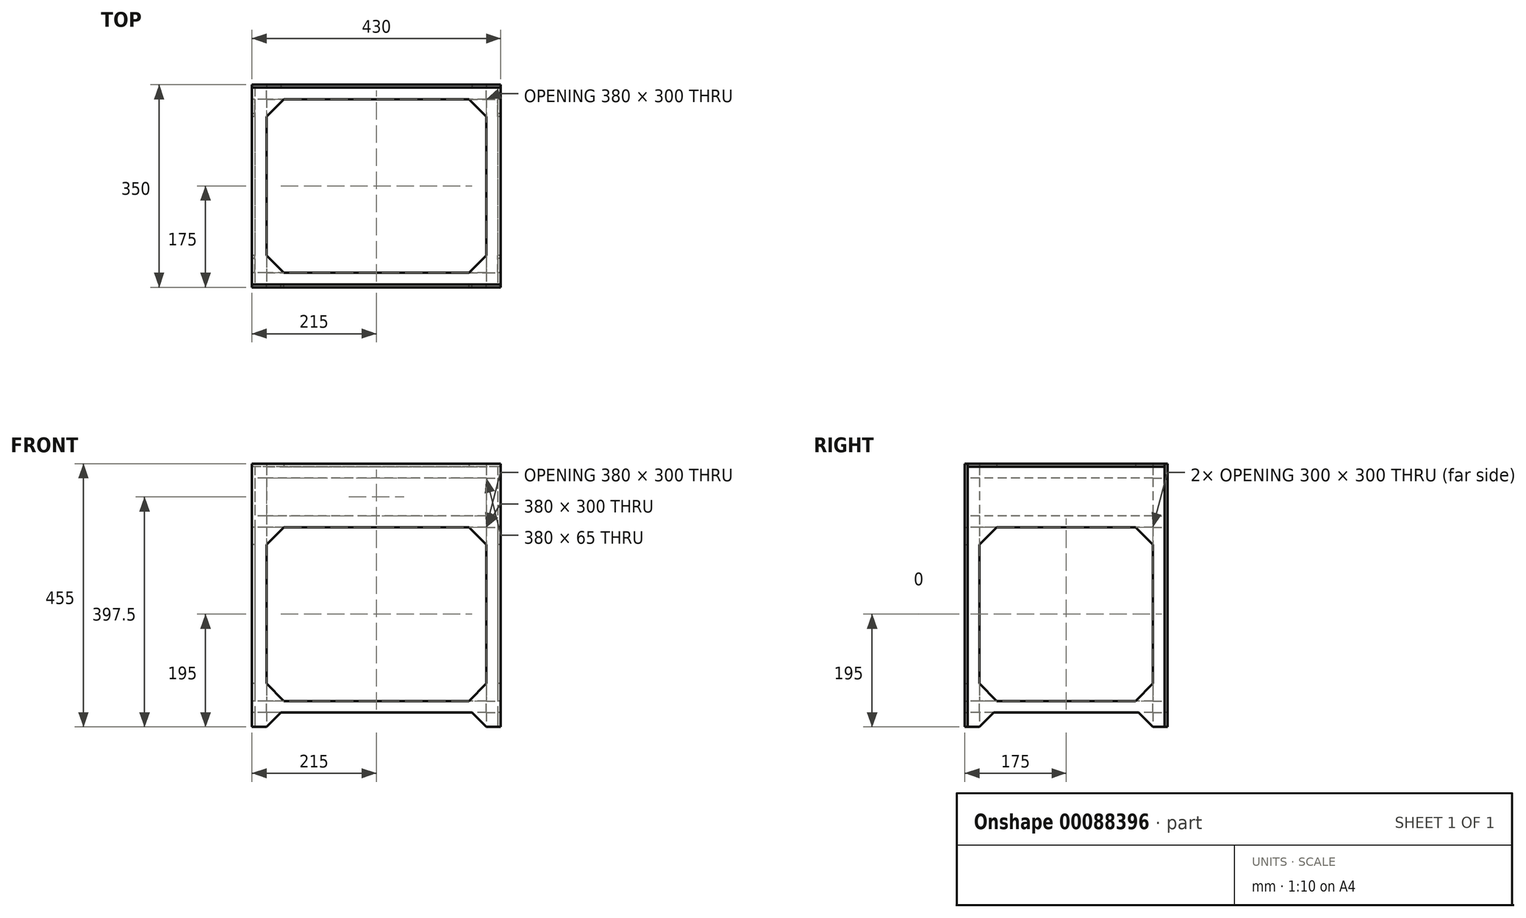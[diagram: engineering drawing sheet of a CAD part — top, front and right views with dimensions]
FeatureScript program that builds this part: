
annotation { "Feature Type Name" : "Feature", "Feature Type Description" : "" }
export const myFeature = defineFeature(function(context is Context, id is Id, definition is map)
    precondition{}
    {
        {
            assignVariable(context, id + "F0", {"name" : "thick", "anyValue" : 5});
        }
        {
            var Q0;
            Q0=qCreatedBy(makeId("Top.planeOp"),FACE);
            var sketch = newSketch(context, id + "F1", { "sketchPlane" : qUnion([Q0])});
            skLineSegment(sketch, "E0.bottom", {"start": v(190, 150) * mm, "end": v(-190, 150) * mm});
            skLineSegment(sketch, "E0.top", {"start": v(190, -150) * mm, "end": v(-190, -150) * mm});
            skLineSegment(sketch, "E0.left", {"start": v(190, 150) * mm, "end": v(190, -150) * mm});
            skLineSegment(sketch, "E0.right", {"start": v(-190, 150) * mm, "end": v(-190, -150) * mm});
            skPoint(sketch, "E0.middle", {"position": v(0, 0) * mm});
            skLineSegment(sketch, "E1.0", {"start": v(210, 170) * mm, "end": v(-210, 170) * mm});
            skLineSegment(sketch, "E1.1", {"start": v(210, 170) * mm, "end": v(210, -170) * mm});
            skLineSegment(sketch, "E1.2", {"start": v(210, -170) * mm, "end": v(-210, -170) * mm});
            skLineSegment(sketch, "E1.3", {"start": v(-210, 170) * mm, "end": v(-210, -170) * mm});
            skLineSegment(sketch, "E2", {"start": v(190, -150) * mm, "end": v(190, -170) * mm});
            skLineSegment(sketch, "E3", {"start": v(-190, -150) * mm, "end": v(-190, -170) * mm});
            skLineSegment(sketch, "E4", {"start": v(-190, 150) * mm, "end": v(-190, 170) * mm});
            skLineSegment(sketch, "E5", {"start": v(190, 150) * mm, "end": v(190, 170) * mm});
            skLineSegment(sketch, "E6", {"start": v(190, 150) * mm, "end": v(210, 150) * mm});
            skLineSegment(sketch, "E7", {"start": v(190, -150) * mm, "end": v(210, -150) * mm});
            skLineSegment(sketch, "E8", {"start": v(-190, -150) * mm, "end": v(-210, -150) * mm});
            skLineSegment(sketch, "E9", {"start": v(-190, 150) * mm, "end": v(-210, 150) * mm});
            skSolve(sketch);
        }
        {
            var Q0;
            Q0=makeQuery(id+"F1.imprint","IMPRINT",FACE,{"disambiguationData":[TD([[makeQuery(id+"F1.imprint","IMPRINT",EDGE,{"derivedFrom":sQuery(id+"F1.wireOp",EDGE,"E0.right")}),-1.0]])]});
            var Q1;
            Q1=makeQuery(id+"F1.imprint","IMPRINT",FACE,{"disambiguationData":[TD([[makeQuery(id+"F1.imprint","IMPRINT",EDGE,{"derivedFrom":sQuery(id+"F1.wireOp",EDGE,"E0.bottom")}),-1.0]])]});
            var Q2;
            Q2=makeQuery(id+"F1.imprint","IMPRINT",FACE,{"disambiguationData":[TD([[makeQuery(id+"F1.imprint","IMPRINT",EDGE,{"derivedFrom":sQuery(id+"F1.wireOp",EDGE,"E0.left")}),1.0]])]});
            var Q3;
            Q3=makeQuery(id+"F1.imprint","IMPRINT",FACE,{"disambiguationData":[TD([[makeQuery(id+"F1.imprint","IMPRINT",EDGE,{"derivedFrom":sQuery(id+"F1.wireOp",EDGE,"E0.top")}),1.0]])]});
            extrude(context, id + "F2", {"entities" : qUnion([Q0, Q1, Q2, Q3]), "depth" : 20 * mm});
        }
        {
            var Q0;
            {var subQ3=sQuery(id+"F1.wireOp",EDGE,"E3");Q0=makeQuery(id+"F1.imprint","IMPRINT",FACE,{"disambiguationData":[TD([[makeQuery(id+"F1.imprint","IMPRINT",EDGE,{"derivedFrom":subQ3}),-1.0]])]});}
            var Q1;
            {var subQ4=sQuery(id+"F1.wireOp",EDGE,"E2");Q1=makeQuery(id+"F1.imprint","IMPRINT",FACE,{"disambiguationData":[TD([[makeQuery(id+"F1.imprint","IMPRINT",EDGE,{"derivedFrom":subQ4}),1.0]])]});}
            var Q2;
            {var subQ3=sQuery(id+"F1.wireOp",EDGE,"E4");Q2=makeQuery(id+"F1.imprint","IMPRINT",FACE,{"disambiguationData":[TD([[makeQuery(id+"F1.imprint","IMPRINT",EDGE,{"derivedFrom":subQ3}),1.0]])]});}
            var Q3;
            {var subQ3=sQuery(id+"F1.wireOp",EDGE,"E5");Q3=makeQuery(id+"F1.imprint","IMPRINT",FACE,{"disambiguationData":[TD([[makeQuery(id+"F1.imprint","IMPRINT",EDGE,{"derivedFrom":subQ3}),-1.0]])]});}
            extrude(context, id + "F3", {"entities" : qUnion([Q0, Q1, Q2, Q3]), "operationType" : NewBodyOperationType.ADD, "depth" : 105 * mm, "hasSecondDirection" : true, "secondDirectionOppositeDirection" : true, "secondDirectionDepth" : 345 * mm});
        }
        {
            var Q0;
            Q0=makeQuery(id+"F1.imprint","IMPRINT",FACE,{"disambiguationData":[TD([[makeQuery(id+"F1.imprint","IMPRINT",EDGE,{"derivedFrom":sQuery(id+"F1.wireOp",EDGE,"E0.right")}),-1.0]])]});
            var Q1;
            Q1=makeQuery(id+"F1.imprint","IMPRINT",FACE,{"disambiguationData":[TD([[makeQuery(id+"F1.imprint","IMPRINT",EDGE,{"derivedFrom":sQuery(id+"F1.wireOp",EDGE,"E0.bottom")}),-1.0]])]});
            var Q2;
            Q2=makeQuery(id+"F1.imprint","IMPRINT",FACE,{"disambiguationData":[TD([[makeQuery(id+"F1.imprint","IMPRINT",EDGE,{"derivedFrom":sQuery(id+"F1.wireOp",EDGE,"E0.left")}),1.0]])]});
            var Q3;
            Q3=makeQuery(id+"F1.imprint","IMPRINT",FACE,{"disambiguationData":[TD([[makeQuery(id+"F1.imprint","IMPRINT",EDGE,{"derivedFrom":sQuery(id+"F1.wireOp",EDGE,"E0.top")}),1.0]])]});
            var Q4;
            Q4=makeQuery(id+"F3.opExtrude","CAP_FACE",FACE,{"disambiguationData":[OSD([sQuery(id+"F1.wireOp",EDGE,"E1.2"),sQuery(id+"F1.wireOp",EDGE,"E1.3"),sQuery(id+"F1.wireOp",EDGE,"E3"),sQuery(id+"F1.wireOp",EDGE,"E8")])],"isStart":false});
            extrude(context, id + "F4", {"entities" : qUnion([Q0, Q1, Q2, Q3]), "operationType" : NewBodyOperationType.ADD, "endBound" : BoundingType.UP_TO_SURFACE, "endBoundEntityFace" : qUnion([Q4]), "depth" : 50 * mm, "hasSecondDirection" : true, "secondDirectionOppositeDirection" : false, "secondDirectionDepth" : 85 * mm});
        }
        {
            var Q0;
            Q0=makeQuery(id+"F1.imprint","IMPRINT",FACE,{"disambiguationData":[TD([[makeQuery(id+"F1.imprint","IMPRINT",EDGE,{"derivedFrom":sQuery(id+"F1.wireOp",EDGE,"E0.right")}),-1.0]])]});
            var Q1;
            Q1=makeQuery(id+"F1.imprint","IMPRINT",FACE,{"disambiguationData":[TD([[makeQuery(id+"F1.imprint","IMPRINT",EDGE,{"derivedFrom":sQuery(id+"F1.wireOp",EDGE,"E0.bottom")}),-1.0]])]});
            var Q2;
            Q2=makeQuery(id+"F1.imprint","IMPRINT",FACE,{"disambiguationData":[TD([[makeQuery(id+"F1.imprint","IMPRINT",EDGE,{"derivedFrom":sQuery(id+"F1.wireOp",EDGE,"E0.left")}),1.0]])]});
            var Q3;
            Q3=makeQuery(id+"F1.imprint","IMPRINT",FACE,{"disambiguationData":[TD([[makeQuery(id+"F1.imprint","IMPRINT",EDGE,{"derivedFrom":sQuery(id+"F1.wireOp",EDGE,"E0.top")}),1.0]])]});
            extrude(context, id + "F5", {"entities" : qUnion([Q0, Q1, Q2, Q3]), "operationType" : NewBodyOperationType.ADD, "oppositeDirection" : true, "depth" : 320 * mm, "hasSecondDirection" : true, "secondDirectionOppositeDirection" : true, "secondDirectionDepth" : 300 * mm});
        }
        {
            var Q0;
            {var subQ0=sQuery(id+"F1.wireOp",EDGE,"E1.2");Q0=makeQuery(id+"F5.boolean.opBoolean","MERGE",FACE,{"derivedFrom":[makeQuery(id+"F4.boolean.opBoolean","MERGE",FACE,{"derivedFrom":[makeQuery(id+"F3.boolean.opBoolean","MERGE",FACE,{"derivedFrom":[makeQuery(id+"F2.opExtrude","SWEPT_FACE",FACE,{"disambiguationData":[OSD([subQ0])]}),makeQuery(id+"F3.opExtrude","SWEPT_FACE",FACE,{"disambiguationData":[OSD([subQ0]),TDD([makeQuery(id+"F1.imprint","IMPRINT",EDGE,{"disambiguationData":[TD([[makeQuery(id+"F1.imprint","INTERSECT",VERTEX,{"derivedFrom":[sQuery(id+"F1.wireOp",EDGE,"E1.1"),subQ0]}),-1.0]])],"derivedFrom":subQ0})])]}),makeQuery(id+"F3.opExtrude","SWEPT_FACE",FACE,{"disambiguationData":[OSD([subQ0]),TDD([makeQuery(id+"F1.imprint","IMPRINT",EDGE,{"disambiguationData":[TD([[makeQuery(id+"F1.imprint","INTERSECT",VERTEX,{"derivedFrom":[subQ0,sQuery(id+"F1.wireOp",EDGE,"E1.3")]}),1.0]])],"derivedFrom":subQ0})])]})]}),makeQuery(id+"F4.opExtrude","SWEPT_FACE",FACE,{"disambiguationData":[OSD([subQ0])]})]}),makeQuery(id+"F5.opExtrude","SWEPT_FACE",FACE,{"disambiguationData":[OSD([subQ0])]})]});}
            var sketch = newSketch(context, id + "F6", { "sketchPlane" : qUnion([Q0])});
            skLineSegment(sketch, "E10.0.0", {"start": v(-190, -320) * mm, "end": v(190, -320) * mm});
            skLineSegment(sketch, "E10.0.1", {"start": v(190, -320) * mm, "end": v(190, -345) * mm});
            skLineSegment(sketch, "E10.0.2", {"start": v(190, -345) * mm, "end": v(210, -345) * mm});
            skLineSegment(sketch, "E10.0.3", {"start": v(210, -345) * mm, "end": v(210, 105) * mm});
            skLineSegment(sketch, "E10.0.4", {"start": v(210, 105) * mm, "end": v(-210, 105) * mm});
            skLineSegment(sketch, "E10.0.5", {"start": v(-210, 105) * mm, "end": v(-210, -345) * mm});
            skLineSegment(sketch, "E10.0.6", {"start": v(-210, -345) * mm, "end": v(-190, -345) * mm});
            skLineSegment(sketch, "E10.0.7", {"start": v(-190, -345) * mm, "end": v(-190, -320) * mm});
            skLineSegment(sketch, "E11.0", {"start": v(190, 85) * mm, "end": v(-190, 85) * mm});
            skLineSegment(sketch, "E12.0", {"start": v(-190, 85) * mm, "end": v(-190, 20) * mm});
            skLineSegment(sketch, "E13.0", {"start": v(190, 20) * mm, "end": v(-190, 20) * mm});
            skLineSegment(sketch, "E14.0", {"start": v(190, 85) * mm, "end": v(190, 20) * mm});
            skLineSegment(sketch, "E15.0", {"start": v(-190, 0) * mm, "end": v(-190, -300) * mm});
            skLineSegment(sketch, "E16.0", {"start": v(190, -300) * mm, "end": v(-190, -300) * mm});
            skLineSegment(sketch, "E17.0", {"start": v(190, 0) * mm, "end": v(190, -300) * mm});
            skLineSegment(sketch, "E18", {"start": v(-160, 0) * mm, "end": v(-190, -30) * mm});
            skLineSegment(sketch, "E19", {"start": v(160, 0) * mm, "end": v(190, -30) * mm});
            skLineSegment(sketch, "E20", {"start": v(190, -270) * mm, "end": v(160, -300) * mm});
            skLineSegment(sketch, "E21", {"start": v(-190, -270) * mm, "end": v(-160, -300) * mm});
            skLineSegment(sketch, "E22", {"start": v(-165, -320) * mm, "end": v(-190, -345) * mm});
            skLineSegment(sketch, "E23", {"start": v(165, -320) * mm, "end": v(190, -345) * mm});
            skLineSegment(sketch, "E24.0", {"start": v(-215, 110) * mm, "end": v(-215, -345) * mm});
            skLineSegment(sketch, "E24.1", {"start": v(215, 110) * mm, "end": v(-215, 110) * mm});
            skLineSegment(sketch, "E24.2", {"start": v(215, -345) * mm, "end": v(215, 110) * mm});
            skLineSegment(sketch, "E25", {"start": v(-215, -345) * mm, "end": v(-210, -345) * mm});
            skLineSegment(sketch, "E26", {"start": v(210, -345) * mm, "end": v(215, -345) * mm});
            skLineSegment(sketch, "E27.0", {"start": v(190, 0) * mm, "end": v(-190, 0) * mm});
            skSolve(sketch);
        }
        {
            var Q0;
            {var subQ20=sQuery(id+"F6.wireOp",EDGE,"E10.0.1");Q0=makeQuery(id+"F6.imprint","IMPRINT",FACE,{"disambiguationData":[TD([[makeQuery(id+"F6.imprint","IMPRINT",EDGE,{"derivedFrom":subQ20}),1.0]])]});}
            var Q1;
            Q1=makeQuery(id+"F6.imprint","IMPRINT",FACE,{"disambiguationData":[TD([[makeQuery(id+"F6.imprint","IMPRINT",EDGE,{"derivedFrom":sQuery(id+"F6.wireOp",EDGE,"E10.0.3")}),1.0]])]});
            var Q2;
            {var subQ3=sQuery(id+"F6.wireOp",EDGE,"E19");Q2=makeQuery(id+"F6.imprint","IMPRINT",FACE,{"disambiguationData":[TD([[makeQuery(id+"F6.imprint","IMPRINT",EDGE,{"derivedFrom":subQ3}),1.0]])]});}
            var Q3;
            {var subQ3=sQuery(id+"F6.wireOp",EDGE,"E18");Q3=makeQuery(id+"F6.imprint","IMPRINT",FACE,{"disambiguationData":[TD([[makeQuery(id+"F6.imprint","IMPRINT",EDGE,{"derivedFrom":subQ3}),-1.0]])]});}
            var Q4;
            {var subQ3=sQuery(id+"F6.wireOp",EDGE,"E20");Q4=makeQuery(id+"F6.imprint","IMPRINT",FACE,{"disambiguationData":[TD([[makeQuery(id+"F6.imprint","IMPRINT",EDGE,{"derivedFrom":subQ3}),1.0]])]});}
            var Q5;
            {var subQ0=sQuery(id+"F6.wireOp",EDGE,"E10.0.1");Q5=makeQuery(id+"F6.imprint","IMPRINT",FACE,{"disambiguationData":[TD([[makeQuery(id+"F6.imprint","IMPRINT",EDGE,{"derivedFrom":subQ0}),-1.0]])]});}
            var Q6;
            {var subQ3=sQuery(id+"F6.wireOp",EDGE,"E21");Q6=makeQuery(id+"F6.imprint","IMPRINT",FACE,{"disambiguationData":[TD([[makeQuery(id+"F6.imprint","IMPRINT",EDGE,{"derivedFrom":subQ3}),-1.0]])]});}
            var Q7;
            {var subQ0=sQuery(id+"F6.wireOp",EDGE,"E10.0.7");Q7=makeQuery(id+"F6.imprint","IMPRINT",FACE,{"disambiguationData":[TD([[makeQuery(id+"F6.imprint","IMPRINT",EDGE,{"derivedFrom":subQ0}),1.0]])]});}
            var Q8;
            Q8=makeQuery(id+"F6.imprint","IMPRINT",FACE,{"disambiguationData":[TD([[makeQuery(id+"F6.imprint","IMPRINT",EDGE,{"derivedFrom":sQuery(id+"F6.wireOp",EDGE,"E11.0")}),1.0]])]});
            extrude(context, id + "F7", {"entities" : qUnion([Q0, Q1, Q2, Q3, Q4, Q5, Q6, Q7, Q8]), "depth" : (getVariable(context, 'thick')) * mm});
        }
        {
            var Q0;
            {var subQ0=sQuery(id+"F1.wireOp",EDGE,"E1.0");Q0=makeQuery(id+"F5.boolean.opBoolean","MERGE",FACE,{"derivedFrom":[makeQuery(id+"F4.boolean.opBoolean","MERGE",FACE,{"derivedFrom":[makeQuery(id+"F3.boolean.opBoolean","MERGE",FACE,{"derivedFrom":[makeQuery(id+"F2.opExtrude","SWEPT_FACE",FACE,{"disambiguationData":[OSD([subQ0])]}),makeQuery(id+"F3.opExtrude","SWEPT_FACE",FACE,{"disambiguationData":[OSD([subQ0]),TDD([makeQuery(id+"F1.imprint","IMPRINT",EDGE,{"disambiguationData":[TD([[makeQuery(id+"F1.imprint","INTERSECT",VERTEX,{"derivedFrom":[subQ0,sQuery(id+"F1.wireOp",EDGE,"E1.1")]}),-1.0]])],"derivedFrom":subQ0})])]}),makeQuery(id+"F3.opExtrude","SWEPT_FACE",FACE,{"disambiguationData":[OSD([subQ0]),TDD([makeQuery(id+"F1.imprint","IMPRINT",EDGE,{"disambiguationData":[TD([[makeQuery(id+"F1.imprint","INTERSECT",VERTEX,{"derivedFrom":[subQ0,sQuery(id+"F1.wireOp",EDGE,"E1.3")]}),1.0]])],"derivedFrom":subQ0})])]})]}),makeQuery(id+"F4.opExtrude","SWEPT_FACE",FACE,{"disambiguationData":[OSD([subQ0])]})]}),makeQuery(id+"F5.opExtrude","SWEPT_FACE",FACE,{"disambiguationData":[OSD([subQ0])]})]});}
            var sketch = newSketch(context, id + "F8", { "sketchPlane" : qUnion([Q0])});
            skLineSegment(sketch, "E28.0.0", {"start": v(-190, -320) * mm, "end": v(190, -320) * mm});
            skLineSegment(sketch, "E28.0.1", {"start": v(190, -320) * mm, "end": v(190, -345) * mm});
            skLineSegment(sketch, "E28.0.2", {"start": v(190, -345) * mm, "end": v(210, -345) * mm});
            skLineSegment(sketch, "E28.0.3", {"start": v(210, -345) * mm, "end": v(210, 105) * mm});
            skLineSegment(sketch, "E28.0.4", {"start": v(210, 105) * mm, "end": v(-210, 105) * mm});
            skLineSegment(sketch, "E28.0.5", {"start": v(-210, 105) * mm, "end": v(-210, -345) * mm});
            skLineSegment(sketch, "E28.0.6", {"start": v(-210, -345) * mm, "end": v(-190, -345) * mm});
            skLineSegment(sketch, "E28.0.7", {"start": v(-190, -345) * mm, "end": v(-190, -320) * mm});
            skLineSegment(sketch, "E29", {"start": v(190, -345) * mm, "end": v(165, -320) * mm});
            skLineSegment(sketch, "E30", {"start": v(-190, -345) * mm, "end": v(-165, -320) * mm});
            skLineSegment(sketch, "E31.0", {"start": v(-215, 110) * mm, "end": v(-215, -345) * mm});
            skLineSegment(sketch, "E31.1", {"start": v(215, 110) * mm, "end": v(-215, 110) * mm});
            skLineSegment(sketch, "E31.2", {"start": v(215, -345) * mm, "end": v(215, 110) * mm});
            skLineSegment(sketch, "E32", {"start": v(-210, -345) * mm, "end": v(-215, -345) * mm});
            skLineSegment(sketch, "E33", {"start": v(210, -345) * mm, "end": v(215, -345) * mm});
            skSolve(sketch);
        }
        {
            var Q0;
            {var subQ0=sQuery(id+"F8.wireOp",EDGE,"E28.0.1");Q0=makeQuery(id+"F8.imprint","IMPRINT",FACE,{"disambiguationData":[TD([[makeQuery(id+"F8.imprint","IMPRINT",EDGE,{"derivedFrom":subQ0}),1.0]])]});}
            var Q1;
            {var subQ0=sQuery(id+"F1.wireOp",EDGE,"E1.0");Q1=makeQuery(id+"F8.imprint","IMPRINT",FACE,{"disambiguationData":[TD([[makeQuery(id+"F8.imprint","IMPRINT",EDGE,{"derivedFrom":makeQuery(id+"F2.opExtrude","CAP_EDGE",EDGE,{"disambiguationData":[OSD([subQ0])],"isStart":false})}),1.0]])]});}
            var Q2;
            {var subQ0=sQuery(id+"F1.wireOp",EDGE,"E1.0");Q2=makeQuery(id+"F8.imprint","IMPRINT",FACE,{"disambiguationData":[TD([[makeQuery(id+"F8.imprint","IMPRINT",EDGE,{"derivedFrom":makeQuery(id+"F2.opExtrude","CAP_EDGE",EDGE,{"disambiguationData":[OSD([subQ0])],"isStart":true})}),-1.0]])]});}
            var Q3;
            Q3=makeQuery(id+"F8.imprint","IMPRINT",FACE,{"disambiguationData":[TD([[makeQuery(id+"F8.imprint","IMPRINT",EDGE,{"derivedFrom":sQuery(id+"F8.wireOp",EDGE,"E28.0.3")}),1.0]])]});
            var Q4;
            {var subQ0=sQuery(id+"F8.wireOp",EDGE,"E28.0.1");Q4=makeQuery(id+"F8.imprint","IMPRINT",FACE,{"disambiguationData":[TD([[makeQuery(id+"F8.imprint","IMPRINT",EDGE,{"derivedFrom":subQ0}),-1.0]])]});}
            var Q5;
            {var subQ0=sQuery(id+"F8.wireOp",EDGE,"E28.0.7");Q5=makeQuery(id+"F8.imprint","IMPRINT",FACE,{"disambiguationData":[TD([[makeQuery(id+"F8.imprint","IMPRINT",EDGE,{"derivedFrom":subQ0}),1.0]])]});}
            extrude(context, id + "F9", {"entities" : qUnion([Q0, Q1, Q2, Q3, Q4, Q5]), "depth" : (getVariable(context, 'thick')) * mm});
        }
        {
            var Q0;
            {var subQ0=sQuery(id+"F1.wireOp",EDGE,"E9");var subQ1=sQuery(id+"F1.wireOp",EDGE,"E8");var subQ2=sQuery(id+"F1.wireOp",EDGE,"E1.3");var subQ3=sQuery(id+"F1.wireOp",EDGE,"E7");var subQ4=sQuery(id+"F1.wireOp",EDGE,"E6");var subQ5=sQuery(id+"F1.wireOp",EDGE,"E1.1");var subQ6=sQuery(id+"F1.wireOp",EDGE,"E3");var subQ7=sQuery(id+"F1.wireOp",EDGE,"E2");var subQ8=sQuery(id+"F1.wireOp",EDGE,"E1.2");var subQ9=sQuery(id+"F1.wireOp",EDGE,"E5");var subQ10=sQuery(id+"F1.wireOp",EDGE,"E4");var subQ11=sQuery(id+"F1.wireOp",EDGE,"E1.0");Q0=makeQuery(id+"F4.boolean.opBoolean","MERGE",FACE,{"derivedFrom":[makeQuery(id+"F3.opExtrude","CAP_FACE",FACE,{"disambiguationData":[OSD([subQ11,subQ5,subQ9,subQ4])],"isStart":false}),makeQuery(id+"F3.opExtrude","CAP_FACE",FACE,{"disambiguationData":[OSD([subQ11,subQ2,subQ10,subQ0])],"isStart":false}),makeQuery(id+"F3.opExtrude","CAP_FACE",FACE,{"disambiguationData":[OSD([subQ5,subQ8,subQ7,subQ3])],"isStart":false}),makeQuery(id+"F3.opExtrude","CAP_FACE",FACE,{"disambiguationData":[OSD([subQ8,subQ2,subQ6,subQ1])],"isStart":false}),makeQuery(id+"F4.opExtrude","CAP_FACE",FACE,{"disambiguationData":[OSD([sQuery(id+"F1.wireOp",EDGE,"E0.bottom"),subQ11,subQ10,subQ9])],"isStart":false}),makeQuery(id+"F4.opExtrude","CAP_FACE",FACE,{"disambiguationData":[OSD([sQuery(id+"F1.wireOp",EDGE,"E0.top"),subQ8,subQ7,subQ6])],"isStart":false}),makeQuery(id+"F4.opExtrude","CAP_FACE",FACE,{"disambiguationData":[OSD([sQuery(id+"F1.wireOp",EDGE,"E0.left"),subQ5,subQ4,subQ3])],"isStart":false}),makeQuery(id+"F4.opExtrude","CAP_FACE",FACE,{"disambiguationData":[OSD([sQuery(id+"F1.wireOp",EDGE,"E0.right"),subQ2,subQ1,subQ0])],"isStart":false})]});}
            var sketch = newSketch(context, id + "F10", { "sketchPlane" : qUnion([Q0])});
            skLineSegment(sketch, "E34.0.0", {"start": v(210, -170) * mm, "end": v(210, 170) * mm});
            skLineSegment(sketch, "E34.0.1", {"start": v(210, 170) * mm, "end": v(-210, 170) * mm});
            skLineSegment(sketch, "E34.0.2", {"start": v(-210, 170) * mm, "end": v(-210, -170) * mm});
            skLineSegment(sketch, "E34.0.3", {"start": v(-210, -170) * mm, "end": v(210, -170) * mm});
            skLineSegment(sketch, "E35.0", {"start": v(215, -170) * mm, "end": v(215, 170) * mm});
            skLineSegment(sketch, "E36.0", {"start": v(-215, 170) * mm, "end": v(-215, -170) * mm});
            skLineSegment(sketch, "E37", {"start": v(-215, -170) * mm, "end": v(-210, -170) * mm});
            skLineSegment(sketch, "E38", {"start": v(-215, 170) * mm, "end": v(-210, 170) * mm});
            skLineSegment(sketch, "E39", {"start": v(210, 170) * mm, "end": v(215, 170) * mm});
            skLineSegment(sketch, "E40", {"start": v(210, -170) * mm, "end": v(215, -170) * mm});
            skLineSegment(sketch, "E41.0", {"start": v(-190, 150) * mm, "end": v(-190, -150) * mm});
            skLineSegment(sketch, "E42.0", {"start": v(190, -150) * mm, "end": v(-190, -150) * mm});
            skLineSegment(sketch, "E43.0", {"start": v(190, -150) * mm, "end": v(190, 150) * mm});
            skLineSegment(sketch, "E44.0", {"start": v(190, 150) * mm, "end": v(-190, 150) * mm});
            skLineSegment(sketch, "E45", {"start": v(-190, -120) * mm, "end": v(-160, -150) * mm});
            skLineSegment(sketch, "E46", {"start": v(-190, 120) * mm, "end": v(-160, 150) * mm});
            skLineSegment(sketch, "E47", {"start": v(160, 150) * mm, "end": v(190, 120) * mm});
            skLineSegment(sketch, "E48", {"start": v(160, -150) * mm, "end": v(190, -120) * mm});
            skSolve(sketch);
        }
        {
            var Q0;
            Q0=makeQuery(id+"F10.imprint","IMPRINT",FACE,{"disambiguationData":[TD([[makeQuery(id+"F10.imprint","IMPRINT",EDGE,{"derivedFrom":sQuery(id+"F10.wireOp",EDGE,"E34.0.0")}),-1.0]])]});
            var Q1;
            Q1=makeQuery(id+"F10.imprint","IMPRINT",FACE,{"disambiguationData":[TD([[makeQuery(id+"F10.imprint","IMPRINT",EDGE,{"derivedFrom":sQuery(id+"F10.wireOp",EDGE,"E34.0.2")}),-1.0]])]});
            var Q2;
            Q2=makeQuery(id+"F10.imprint","IMPRINT",FACE,{"disambiguationData":[TD([[makeQuery(id+"F10.imprint","IMPRINT",EDGE,{"derivedFrom":sQuery(id+"F10.wireOp",EDGE,"E34.0.0")}),1.0]])]});
            var Q3;
            {var subQ3=sQuery(id+"F10.wireOp",EDGE,"E45");Q3=makeQuery(id+"F10.imprint","IMPRINT",FACE,{"disambiguationData":[TD([[makeQuery(id+"F10.imprint","IMPRINT",EDGE,{"derivedFrom":subQ3}),-1.0]])]});}
            var Q4;
            {var subQ3=sQuery(id+"F10.wireOp",EDGE,"E46");Q4=makeQuery(id+"F10.imprint","IMPRINT",FACE,{"disambiguationData":[TD([[makeQuery(id+"F10.imprint","IMPRINT",EDGE,{"derivedFrom":subQ3}),1.0]])]});}
            var Q5;
            {var subQ3=sQuery(id+"F10.wireOp",EDGE,"E47");Q5=makeQuery(id+"F10.imprint","IMPRINT",FACE,{"disambiguationData":[TD([[makeQuery(id+"F10.imprint","IMPRINT",EDGE,{"derivedFrom":subQ3}),1.0]])]});}
            var Q6;
            {var subQ3=sQuery(id+"F10.wireOp",EDGE,"E48");Q6=makeQuery(id+"F10.imprint","IMPRINT",FACE,{"disambiguationData":[TD([[makeQuery(id+"F10.imprint","IMPRINT",EDGE,{"derivedFrom":subQ3}),-1.0]])]});}
            extrude(context, id + "F11", {"entities" : qUnion([Q0, Q1, Q2, Q3, Q4, Q5, Q6]), "depth" : (getVariable(context, 'thick')) * mm});
        }
        {
            var Q0;
            {var subQ0=sQuery(id+"F1.wireOp",EDGE,"E1.1");Q0=makeQuery(id+"F5.boolean.opBoolean","MERGE",FACE,{"derivedFrom":[makeQuery(id+"F4.boolean.opBoolean","MERGE",FACE,{"derivedFrom":[makeQuery(id+"F3.boolean.opBoolean","MERGE",FACE,{"derivedFrom":[makeQuery(id+"F2.opExtrude","SWEPT_FACE",FACE,{"disambiguationData":[OSD([subQ0])]}),makeQuery(id+"F3.opExtrude","SWEPT_FACE",FACE,{"disambiguationData":[OSD([subQ0]),TDD([makeQuery(id+"F1.imprint","IMPRINT",EDGE,{"disambiguationData":[TD([[makeQuery(id+"F1.imprint","INTERSECT",VERTEX,{"derivedFrom":[sQuery(id+"F1.wireOp",EDGE,"E1.0"),subQ0]}),-1.0]])],"derivedFrom":subQ0})])]}),makeQuery(id+"F3.opExtrude","SWEPT_FACE",FACE,{"disambiguationData":[OSD([subQ0]),TDD([makeQuery(id+"F1.imprint","IMPRINT",EDGE,{"disambiguationData":[TD([[makeQuery(id+"F1.imprint","INTERSECT",VERTEX,{"derivedFrom":[subQ0,sQuery(id+"F1.wireOp",EDGE,"E1.2")]}),1.0]])],"derivedFrom":subQ0})])]})]}),makeQuery(id+"F4.opExtrude","SWEPT_FACE",FACE,{"disambiguationData":[OSD([subQ0])]})]}),makeQuery(id+"F5.opExtrude","SWEPT_FACE",FACE,{"disambiguationData":[OSD([subQ0])]})]});}
            var sketch = newSketch(context, id + "F12", { "sketchPlane" : qUnion([Q0])});
            skLineSegment(sketch, "E49.0.0", {"start": v(-150, -320) * mm, "end": v(150, -320) * mm});
            skLineSegment(sketch, "E49.0.1", {"start": v(150, -320) * mm, "end": v(150, -345) * mm});
            skLineSegment(sketch, "E49.0.2", {"start": v(150, -345) * mm, "end": v(170, -345) * mm});
            skLineSegment(sketch, "E49.0.3", {"start": v(170, -345) * mm, "end": v(170, 105) * mm});
            skLineSegment(sketch, "E49.0.4", {"start": v(170, 105) * mm, "end": v(-170, 105) * mm});
            skLineSegment(sketch, "E49.0.5", {"start": v(-170, 105) * mm, "end": v(-170, -345) * mm});
            skLineSegment(sketch, "E49.0.6", {"start": v(-170, -345) * mm, "end": v(-150, -345) * mm});
            skLineSegment(sketch, "E49.0.7", {"start": v(-150, -345) * mm, "end": v(-150, -320) * mm});
            skLineSegment(sketch, "E50", {"start": v(-150, -345) * mm, "end": v(-125, -320) * mm});
            skLineSegment(sketch, "E51", {"start": v(125, -320) * mm, "end": v(150, -345) * mm});
            skLineSegment(sketch, "E52", {"start": v(-150, -270) * mm, "end": v(-120, -300) * mm});
            skLineSegment(sketch, "E53", {"start": v(150, -270) * mm, "end": v(120, -300) * mm});
            skLineSegment(sketch, "E54", {"start": v(120, 0) * mm, "end": v(150, -30) * mm});
            skLineSegment(sketch, "E55", {"start": v(-120, 0) * mm, "end": v(-150, -30) * mm});
            skLineSegment(sketch, "E56.0", {"start": v(-150, 0) * mm, "end": v(-150, -300) * mm});
            skLineSegment(sketch, "E57.0", {"start": v(150, 0) * mm, "end": v(-150, 0) * mm});
            skLineSegment(sketch, "E58.0", {"start": v(150, 0) * mm, "end": v(150, -300) * mm});
            skLineSegment(sketch, "E59.0", {"start": v(150, -300) * mm, "end": v(-150, -300) * mm});
            skSolve(sketch);
        }
        {
            var Q0;
            {var subQ30=sQuery(id+"F12.wireOp",EDGE,"E49.0.1");Q0=makeQuery(id+"F12.imprint","IMPRINT",FACE,{"disambiguationData":[TD([[makeQuery(id+"F12.imprint","IMPRINT",EDGE,{"derivedFrom":subQ30}),1.0]])]});}
            var Q1;
            {var subQ0=sQuery(id+"F1.wireOp",EDGE,"E1.1");Q1=makeQuery(id+"F12.imprint","IMPRINT",FACE,{"disambiguationData":[TD([[makeQuery(id+"F12.imprint","IMPRINT",EDGE,{"derivedFrom":makeQuery(id+"F2.opExtrude","CAP_EDGE",EDGE,{"disambiguationData":[OSD([subQ0])],"isStart":false})}),-1.0]])]});}
            var Q2;
            {var subQ0=sQuery(id+"F12.wireOp",EDGE,"E55");Q2=makeQuery(id+"F12.imprint","IMPRINT",FACE,{"disambiguationData":[TD([[makeQuery(id+"F12.imprint","IMPRINT",EDGE,{"derivedFrom":subQ0}),-1.0]])]});}
            var Q3;
            {var subQ0=sQuery(id+"F12.wireOp",EDGE,"E54");Q3=makeQuery(id+"F12.imprint","IMPRINT",FACE,{"disambiguationData":[TD([[makeQuery(id+"F12.imprint","IMPRINT",EDGE,{"derivedFrom":subQ0}),1.0]])]});}
            var Q4;
            {var subQ0=sQuery(id+"F12.wireOp",EDGE,"E53");Q4=makeQuery(id+"F12.imprint","IMPRINT",FACE,{"disambiguationData":[TD([[makeQuery(id+"F12.imprint","IMPRINT",EDGE,{"derivedFrom":subQ0}),1.0]])]});}
            var Q5;
            {var subQ0=sQuery(id+"F12.wireOp",EDGE,"E52");Q5=makeQuery(id+"F12.imprint","IMPRINT",FACE,{"disambiguationData":[TD([[makeQuery(id+"F12.imprint","IMPRINT",EDGE,{"derivedFrom":subQ0}),-1.0]])]});}
            var Q6;
            {var subQ0=sQuery(id+"F12.wireOp",EDGE,"E49.0.7");Q6=makeQuery(id+"F12.imprint","IMPRINT",FACE,{"disambiguationData":[TD([[makeQuery(id+"F12.imprint","IMPRINT",EDGE,{"derivedFrom":subQ0}),1.0]])]});}
            var Q7;
            {var subQ0=sQuery(id+"F12.wireOp",EDGE,"E49.0.1");Q7=makeQuery(id+"F12.imprint","IMPRINT",FACE,{"disambiguationData":[TD([[makeQuery(id+"F12.imprint","IMPRINT",EDGE,{"derivedFrom":subQ0}),-1.0]])]});}
            extrude(context, id + "F13", {"entities" : qUnion([Q0, Q1, Q2, Q3, Q4, Q5, Q6, Q7]), "depth" : (getVariable(context, 'thick')) * mm});
        }
        {
            var Q0;
            Q0=makeQuery(id+"F13.opExtrude","SWEPT_BODY",BODY,{"disambiguationData":[OSD([sQuery(id+"F12.wireOp",EDGE,"E49.0.0"),sQuery(id+"F12.wireOp",EDGE,"E49.0.2"),sQuery(id+"F12.wireOp",EDGE,"E49.0.3"),sQuery(id+"F12.wireOp",EDGE,"E49.0.4"),sQuery(id+"F12.wireOp",EDGE,"E49.0.5"),sQuery(id+"F12.wireOp",EDGE,"E49.0.6"),sQuery(id+"F12.wireOp",EDGE,"E50"),sQuery(id+"F12.wireOp",EDGE,"E51"),sQuery(id+"F12.wireOp",EDGE,"E52"),sQuery(id+"F12.wireOp",EDGE,"E53"),sQuery(id+"F12.wireOp",EDGE,"E54"),sQuery(id+"F12.wireOp",EDGE,"E55"),sQuery(id+"F12.wireOp",EDGE,"E56.0"),sQuery(id+"F12.wireOp",EDGE,"E57.0"),sQuery(id+"F12.wireOp",EDGE,"E58.0"),sQuery(id+"F12.wireOp",EDGE,"E59.0")])]});
            var Q1;
            Q1=makeQuery(id+"F7.opExtrude","CAP_EDGE",EDGE,{"disambiguationData":[OSD([sQuery(id+"F6.wireOp",EDGE,"E24.1")])],"isStart":false});
            var Q2;
            Q2=makeQuery(id+"F7.opExtrude","CAP_EDGE",EDGE,{"disambiguationData":[OSD([sQuery(id+"F6.wireOp",EDGE,"E24.1")])],"isStart":false});
            transform(context, id + "F14", {"entities" : qUnion([Q0]), "transformType" : TransformType.TRANSLATION_DISTANCE, "transformDirection" : qUnion([Q2]), "distance" : ((getVariable(context, 'thick')) + 420) * mm, "makeCopy" : true});
        }
    });
